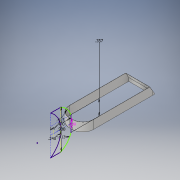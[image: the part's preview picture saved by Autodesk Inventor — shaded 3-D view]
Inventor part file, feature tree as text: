
AUTODESK INVENTOR PART (.ipt)
format: ipt  version: 2018.3 (Build 223284000, 284)  size: 177,152 bytes
history: native  units: in
note: dims shown in document units (in); Inventor stores cm internally (conversion verified against a paired STEP export)
features: sketch x5, extrude x3, plane x2, chamfer x1, mirror x1, thicken_offset x1
ambient origin geometry x8: Origin, YZ Plane, XZ Plane, XY Plane, X Axis, Y Axis, Z Axis, Center Point
bodies: Solid1 (feature_tree)
feature tree (13):
  sketch  "Sketch2"  dims[d1=2.052in d2=15.0deg]
  extrude  "Extrusion1"  TaperAngle=15.0deg  [1 undecoded]
  chamfer  "Chamfer1"  Distance=0.033in
  plane  "Work Plane1"
  extrude  "Extrusion2"  Depth=0.199in
  mirror  "Mirror1"
  thicken_offset  "Thicken1"
  plane  "Work Plane3"
  extrude  "Extrusion3"  Depth=0.199in
  sketch  "Sketch8"  dims[d6=0.2815in d7=0.033in d9=0.0033in d10=1.6552in d11=0.199in d12=0.0in d13=0.1875in d14=0.1875in d15=30.0deg d16=0.0in d17=0.003in d18=0.0in d19=0.0058in d20=0.0058in d23=-0.3125in d24=1.0in d25=0.0in d26=0.199in d27=0.357in d28=0.9in d29=0.413in d30=0.413in d31=0.47in d32=0.24in]
  sketch  "Sketch3"  dims[d3=0.199in]
  sketch  "Sketch4"  dims[d4=1.655in]
  sketch  "Sketch6"  dims[d5=0.2775in]
note: 1 required parameter value undecoded (feature->parameter linkage not recoverable at this tier; creation-order binding heuristic only, values carry confidence <= 0.55)
